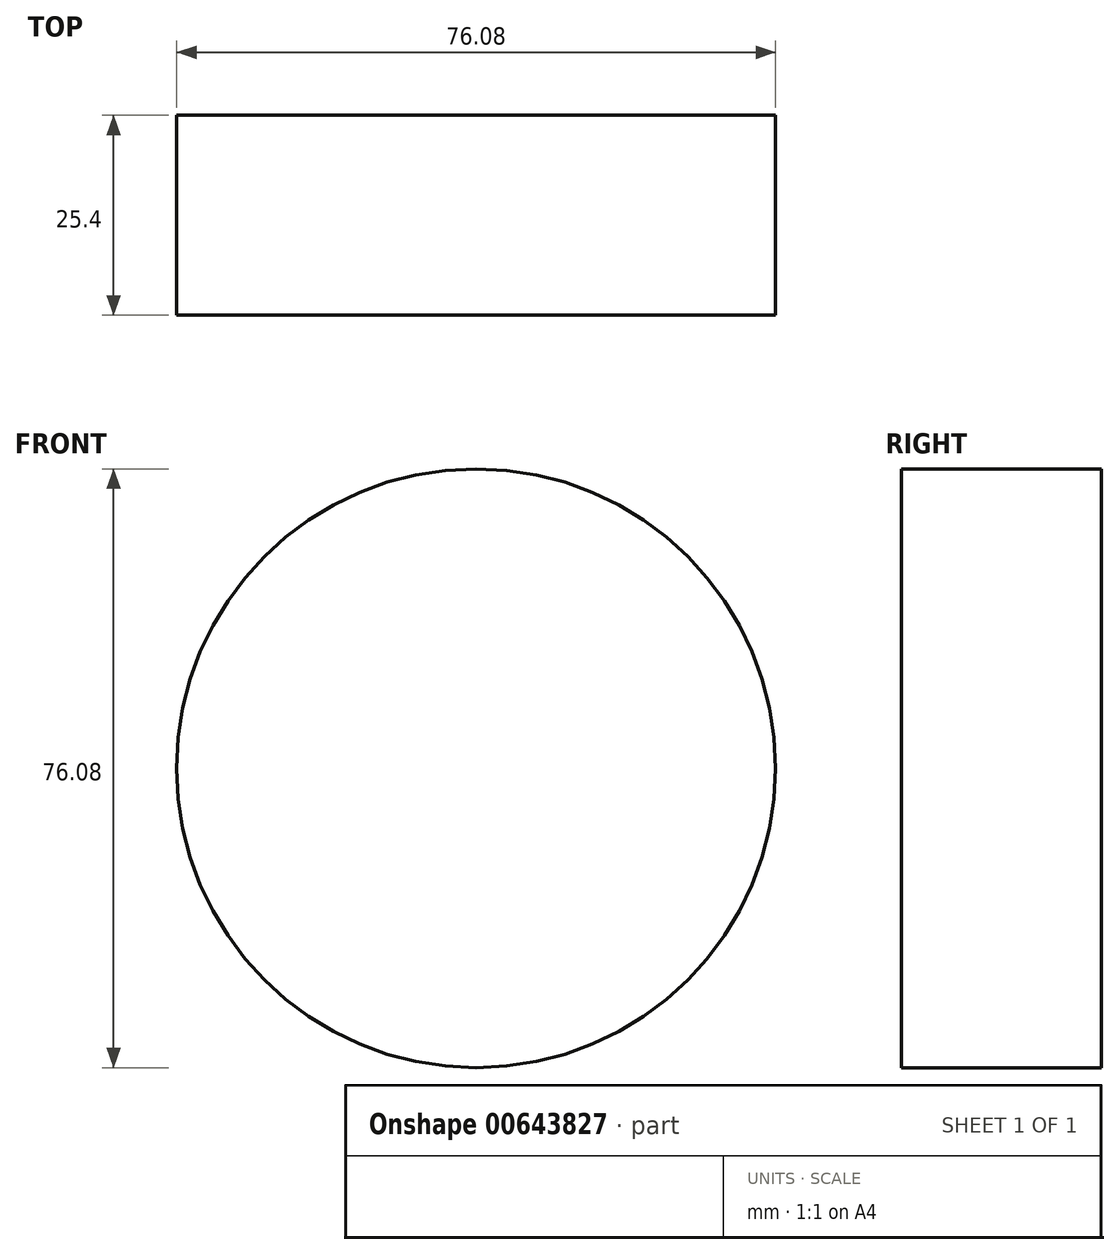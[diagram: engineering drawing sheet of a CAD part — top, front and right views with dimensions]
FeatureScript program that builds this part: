
annotation { "Feature Type Name" : "Feature", "Feature Type Description" : "" }
export const myFeature = defineFeature(function(context is Context, id is Id, definition is map)
    precondition{}
    {
        {
            var Q0;
            Q0=qCreatedBy(makeId("Front.planeOp"),FACE);
            var sketch = newSketch(context, id + "F0", { "sketchPlane" : qUnion([Q0])});
            skCircle(sketch, "E0", {"center": v(0, 0) * mm, "radius": 38.04 * mm});
            skSolve(sketch);
        }
        {
            var Q0;
            Q0 = qSketchRegion(id + "F0", true);
            extrude(context, id + "F1", {"entities" : qUnion([Q0]), "depth" : 25.4 * mm, "offsetDistance" : 25.4 * mm});
        }
    });
